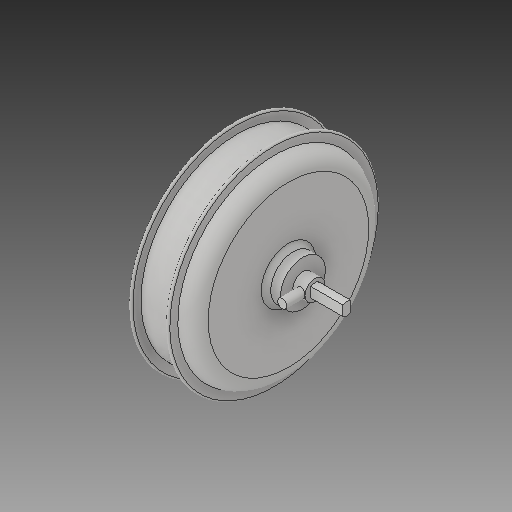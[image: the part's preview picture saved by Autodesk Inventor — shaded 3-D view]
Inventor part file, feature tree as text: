
AUTODESK INVENTOR PART (.ipt)
format: ipt  version: 2019.2 (Build 232265000, 265)  size: 297,472 bytes
history: native  units: mm
features: sketch x6, extrude x5, fillet x4, projected_geometry x2, revolve x1
ambient origin geometry x8: Origin, YZ Plane, XZ Plane, XY Plane, X Axis, Y Axis, Z Axis, Center Point
bodies: Solid1 (feature_tree), Solid4 (feature_tree), Solid5 (feature_tree)
feature tree (18):
  revolve  "Revolution1"  [1 undecoded]
  fillet  "Fillet1"  Radius=46.0mm
  fillet  "Fillet2"  Radius=8.5mm
  fillet  "Fillet4"  Radius=14.25mm
  fillet  "Fillet6"  Radius=23.75mm
  extrude  "Extrusion1"  Depth=40.0mm
  extrude  "Extrusion2"  Depth=12.0mm
  extrude  "Extrusion5"  Depth=50.0mm
  extrude  "Extrusion6"  Depth=36.0mm
  extrude  "Extrusion7"  Depth=12.5mm
  sketch  "Sketch1"  dims[d0=8.0mm d1=8.0mm d2=46.0mm d3=8.5mm d4=14.25mm d5=23.75mm]
  sketch  "Sketch2"  dims[d6=22.5mm d7=40.0mm]
  sketch  "Sketch3"  dims[d8=4.0mm d9=12.0mm]
  sketch  "Sketch6"  dims[d11=4.0mm d12=50.0mm]
  projected_geometry  "Projected Loop3"
  sketch  "Sketch7"  dims[d14=28.0mm d16=36.0mm]
  projected_geometry  "Projected Loop4"
  sketch  "Sketch9"  dims[d18=15.0mm d19=12.5mm d20=40.0mm d21=18.0mm d22=147.0mm d24=90.0deg d25=20.0mm d26=6.0mm d28=2.0mm d29=10.0mm d30=20.0mm d31=8.0mm d32=10.0mm d33=0.0mm d34=10.0mm d35=0.0mm d37=6.0mm d38=120.0mm d44=0.7mm d45=4.0mm d46=0.0mm d47=4.0mm d48=0.0mm d49=11.5mm d50=30.0mm d51=0.0mm d52=76.0mm d54=8.0mm d55=79.0mm d56=155.0mm]
note: 1 required parameter value undecoded (feature->parameter linkage not recoverable at this tier; creation-order binding heuristic only, values carry confidence <= 0.55)
